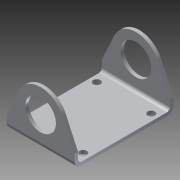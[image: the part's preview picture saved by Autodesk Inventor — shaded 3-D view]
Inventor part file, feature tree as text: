
AUTODESK INVENTOR PART (.ipt)
format: ipt  version: 2013 (Build 170138000, 138)  size: 162,816 bytes
history: native  units: in
note: dims shown in document units (in); Inventor stores cm internally (conversion verified against a paired STEP export)
features: sheet_metal_op x4, sketch x4, other x4
ambient origin geometry x8: Origin, YZ Plane, XZ Plane, XY Plane, X Axis, Y Axis, Z Axis, Center Point
bodies: Solid1 (feature_tree)
feature tree (12):
  sheet_metal_op  "Face1"
  sheet_metal_op  "Flange1"
  sketch  "Sketch1"  dims[d0=3.626in]
  other  "Plate1"
  sketch  "Sketch2"  dims[d2=2.5in]
  other  "Plate2"
  sheet_metal_op  "Bend1"
  sheet_metal_op  "Corner1"
  sketch  "Sketch3"  dims[d3=0.125in]
  sketch  "Sketch4"  dims[d4=0.125in d5=0.0625in d6=0.25in d7=0.125in d8=2.0in d9=90.0deg d10=0.125in d11=0.5in d12=0.125in d13=0.125in d14=1.125in d15=0.25in d16=1.125in d17=1.75in d18=1.25in d19=0.25in d20=100.0in d21=0.0in d22=0.266in d23=0.266in d24=0.266in d25=0.266in d26=1.25in d27=1.25in d28=1.25in d29=1.25in d30=0.25in d31=0.25in d32=0.25in d33=0.25in d34=0.125in d35=0.0in]
  other  "Cut1"
  other  "Cut2"
